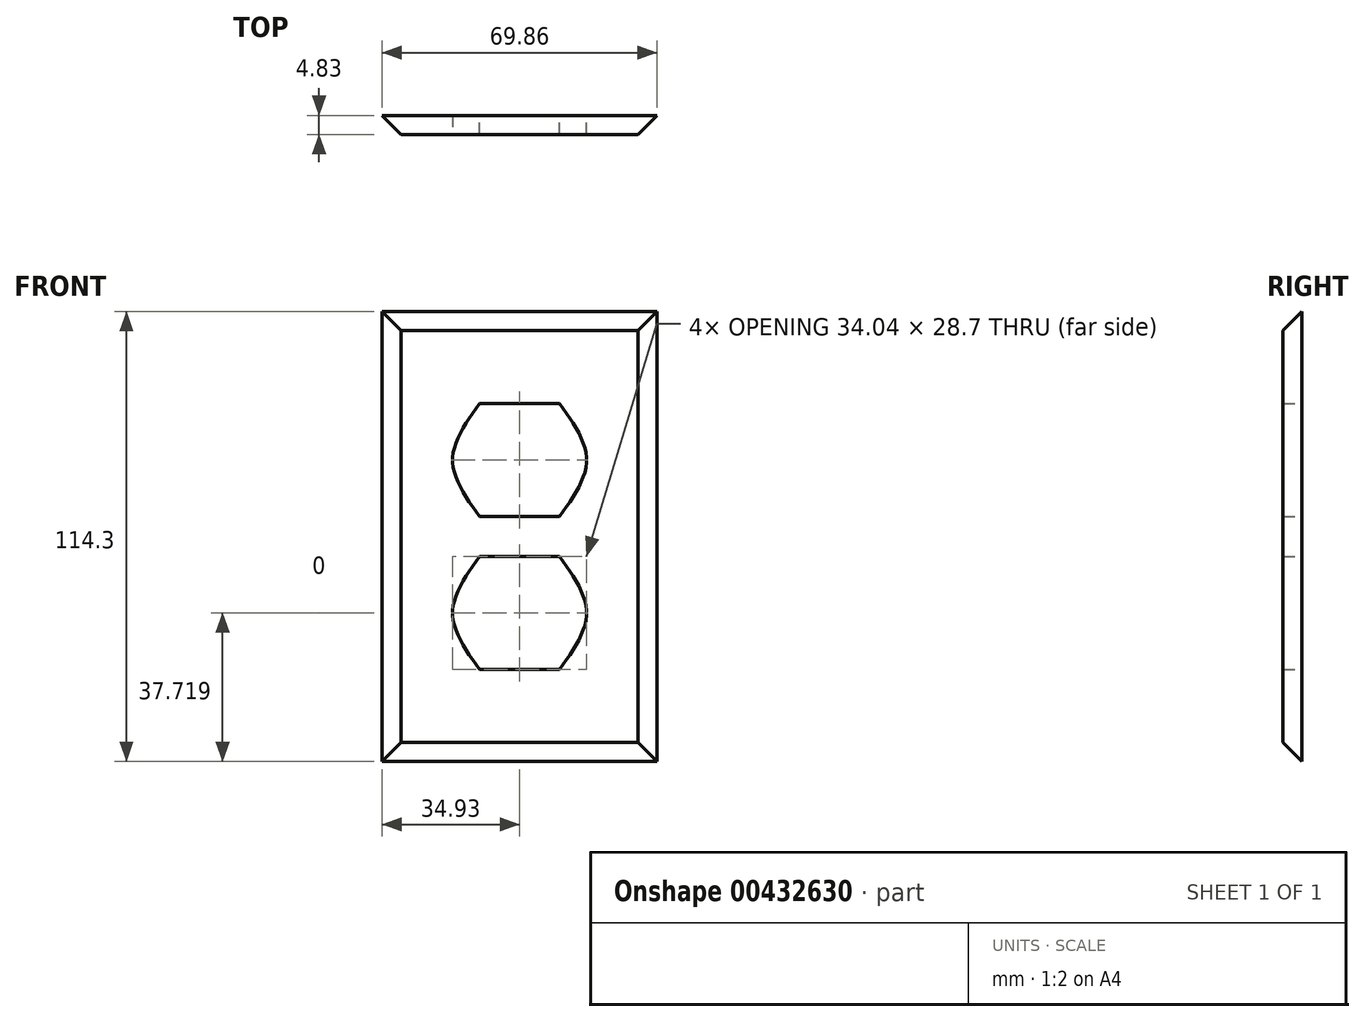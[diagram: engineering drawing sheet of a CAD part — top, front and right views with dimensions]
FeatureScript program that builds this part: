
annotation { "Feature Type Name" : "Feature", "Feature Type Description" : "" }
export const myFeature = defineFeature(function(context is Context, id is Id, definition is map)
    precondition{}
    {
        {
            var Q0;
            Q0=qCreatedBy(makeId("Front.planeOp"),FACE);
            var sketch = newSketch(context, id + "F0", { "sketchPlane" : qUnion([Q0])});
            skLineSegment(sketch, "E0.bottom", {"start": v(-34.92, 57.15) * mm, "end": v(34.93, 57.15) * mm});
            skLineSegment(sketch, "E0.top", {"start": v(-34.93, -57.15) * mm, "end": v(34.92, -57.15) * mm});
            skLineSegment(sketch, "E0.left", {"start": v(-34.92, 57.15) * mm, "end": v(-34.93, -57.15) * mm});
            skLineSegment(sketch, "E0.right", {"start": v(34.93, 57.15) * mm, "end": v(34.92, -57.15) * mm});
            skPoint(sketch, "E0.middle", {"position": v(0, 0) * mm});
            skLineSegment(sketch, "E1.bottom", {"start": v(17.02, 19.43) * mm, "end": v(-17.02, 19.43) * mm, "construction": true});
            skLineSegment(sketch, "E1.top", {"start": v(17.02, -19.43) * mm, "end": v(-17.02, -19.43) * mm, "construction": true});
            skLineSegment(sketch, "E1.left", {"start": v(17.02, 19.43) * mm, "end": v(17.02, -19.43) * mm, "construction": true});
            skLineSegment(sketch, "E1.right", {"start": v(-17.02, 19.43) * mm, "end": v(-17.02, -19.43) * mm, "construction": true});
            skLineSegment(sketch, "E2.bottom", {"start": v(10.16, 33.78) * mm, "end": v(-10.16, 33.78) * mm, "construction": true});
            skLineSegment(sketch, "E2.top", {"start": v(10.16, -33.78) * mm, "end": v(-10.16, -33.78) * mm, "construction": true});
            skLineSegment(sketch, "E2.left", {"start": v(10.16, 33.78) * mm, "end": v(10.16, 19.43) * mm, "construction": true});
            skLineSegment(sketch, "E2.right", {"start": v(-10.16, 33.78) * mm, "end": v(-10.16, 19.43) * mm, "construction": true});
            skLineSegment(sketch, "E3", {"start": v(0, 33.78) * mm, "end": v(0, 19.43) * mm, "construction": true});
            skLineSegment(sketch, "E4", {"start": v(0, 19.43) * mm, "end": v(0, -19.43) * mm, "construction": true});
            skLineSegment(sketch, "E5", {"start": v(0, -19.43) * mm, "end": v(0, -33.78) * mm, "construction": true});
            skPoint(sketch, "E6", {"position": v(-10.16, 19.43) * mm});
            skLineSegment(sketch, "E7", {"start": v(-10.16, 19.43) * mm, "end": v(-10.16, 5.08) * mm, "construction": true});
            skLineSegment(sketch, "E8", {"start": v(-10.16, 5.08) * mm, "end": v(-10.16, -5.08) * mm, "construction": true});
            skLineSegment(sketch, "E9", {"start": v(10.16, 19.43) * mm, "end": v(10.16, 5.08) * mm, "construction": true});
            skLineSegment(sketch, "E10", {"start": v(10.16, 5.08) * mm, "end": v(10.16, -5.08) * mm, "construction": true});
            skLineSegment(sketch, "E11", {"start": v(10.16, -5.08) * mm, "end": v(10.16, -19.43) * mm, "construction": true});
            skLineSegment(sketch, "E12", {"start": v(-10.16, -5.08) * mm, "end": v(-10.16, -19.43) * mm, "construction": true});
            skLineSegment(sketch, "E13", {"start": v(-10.16, -19.43) * mm, "end": v(-10.16, -33.78) * mm, "construction": true});
            skLineSegment(sketch, "E14", {"start": v(10.16, -19.43) * mm, "end": v(10.16, -33.78) * mm, "construction": true});
            skFitSpline(sketch, "E15", {"points": [v(-10.16, 33.78) * mm, v(-17.02, 19.43) * mm, v(-10.16, 5.08) * mm], "startDerivative": vector(-20.57, -28.7) * mm, "endDerivative": vector(20.57, -28.7) * mm});
            skFitSpline(sketch, "E16", {"points": [v(10.16, 33.78) * mm, v(17.02, 19.43) * mm, v(10.16, 5.08) * mm], "startDerivative": vector(20.57, -28.7) * mm, "endDerivative": vector(-20.57, -28.7) * mm});
            skFitSpline(sketch, "E17", {"points": [v(-10.16, -5.08) * mm, v(-17.02, -19.43) * mm, v(-10.16, -33.78) * mm], "startDerivative": vector(-20.57, -28.7) * mm, "endDerivative": vector(20.57, -28.7) * mm});
            skFitSpline(sketch, "E18", {"points": [v(10.16, -5.08) * mm, v(17.02, -19.43) * mm, v(10.16, -33.78) * mm], "startDerivative": vector(20.57, -28.7) * mm, "endDerivative": vector(-20.57, -28.7) * mm});
            skLineSegment(sketch, "E19", {"start": v(-10.16, 33.78) * mm, "end": v(10.16, 33.78) * mm});
            skLineSegment(sketch, "E20", {"start": v(10.16, 5.08) * mm, "end": v(-10.16, 5.08) * mm});
            skLineSegment(sketch, "E21", {"start": v(-10.16, -5.08) * mm, "end": v(10.16, -5.08) * mm});
            skLineSegment(sketch, "E22", {"start": v(10.16, -33.78) * mm, "end": v(-10.16, -33.78) * mm});
            skLineSegment(sketch, "E23", {"start": v(-13.59, 29) * mm, "end": v(-13.59, -29) * mm, "construction": true});
            skSolve(sketch);
        }
        {
            var Q0;
            Q0 = qSketchRegion(id + "F0", true);
            extrude(context, id + "F1", {"entities" : qUnion([Q0]), "depth" : 4.83 * mm});
        }
        {
            var Q0;
            Q0=makeQuery(id+"F1.opExtrude","CAP_EDGE",EDGE,{"disambiguationData":[OSD([sQuery(id+"F0.wireOp",EDGE,"E0.left")])],"isStart":false});
            var Q1;
            Q1=makeQuery(id+"F1.opExtrude","CAP_EDGE",EDGE,{"disambiguationData":[OSD([sQuery(id+"F0.wireOp",EDGE,"E0.bottom")])],"isStart":false});
            var Q2;
            Q2=makeQuery(id+"F1.opExtrude","CAP_EDGE",EDGE,{"disambiguationData":[OSD([sQuery(id+"F0.wireOp",EDGE,"E0.right")])],"isStart":false});
            var Q3;
            Q3=makeQuery(id+"F1.opExtrude","CAP_EDGE",EDGE,{"disambiguationData":[OSD([sQuery(id+"F0.wireOp",EDGE,"E0.top")])],"isStart":false});
            chamfer(context, id + "F2", {"entities" : qUnion([Q0, Q1, Q2, Q3]), "width" : 4.83 * mm, "tangentPropagation" : true});
        }
    });
